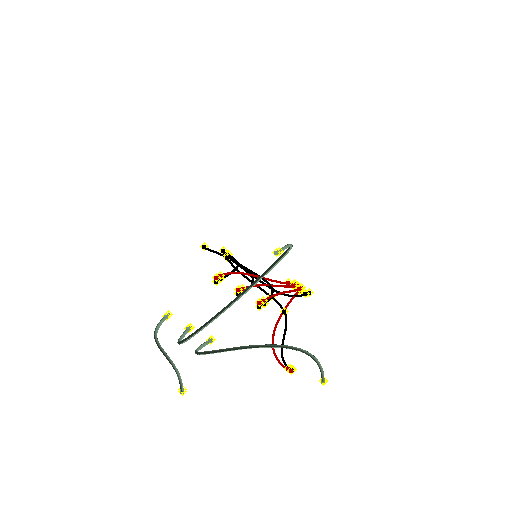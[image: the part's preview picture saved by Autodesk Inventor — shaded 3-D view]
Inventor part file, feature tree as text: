
AUTODESK INVENTOR PART (.ipt)
format: ipt  version: 2022 (Build 260153000, 153)  size: 630,272 bytes
history: native  units: mm (DEFAULTED — no unit token found)
features: other x74, plane x12, sketch x12, sweep x12
ambient origin geometry x8: Origin, YZ Plane, XZ Plane, XY Plane, X Axis, Y Axis, Z Axis, Center Point
bodies: Body1 (feature_tree), Body2 (feature_tree), Body3 (feature_tree), Body4 (feature_tree), Body5 (feature_tree), Body6 (feature_tree), Body7 (feature_tree), Body8 (feature_tree), Body9 (feature_tree), Body10 (feature_tree), Body11 (feature_tree), Body12 (feature_tree)
feature tree (110):
  other  "Work Point1"
  other  "Work Point2"
  other  "Wire1"
  other  "Work Point3"
  other  "Work Point4"
  other  "Wire2"
  other  "Work Point5"
  other  "Work Point6"
  other  "Wire3"
  other  "Work Point7"
  other  "Work Point8"
  other  "Work Point9"
  other  "Work Point10"
  other  "Work Point11"
  other  "Work Point12"
  plane  "Work Plane1"
  plane  "Work Plane2"
  plane  "Work Plane3"
  other  "Work Point13"
  other  "Work Point14"
  other  "Wire4"
  other  "Work Point15"
  other  "Work Point16"
  other  "Wire5"
  other  "Work Point17"
  other  "Work Point18"
  other  "Wire6"
  other  "Work Point19"
  other  "Work Point20"
  other  "Wire7"
  other  "Work Point21"
  other  "Work Point22"
  other  "Wire8"
  other  "Work Point23"
  other  "Work Point24"
  other  "Wire9"
  plane  "Work Plane4"
  plane  "Work Plane5"
  plane  "Work Plane6"
  plane  "Work Plane7"
  plane  "Work Plane8"
  plane  "Work Plane9"
  other  "Work Point25"
  other  "Work Point26"
  other  "Work Point27"
  other  "Work Point28"
  other  "Work Point29"
  other  "Work Point30"
  other  "Work Point31"
  other  "Work Point32"
  other  "Work Point33"
  other  "Work Point34"
  other  "Work Point35"
  other  "Work Point36"
  other  "Work Point37"
  other  "Work Point38"
  other  "Wire10"
  plane  "Work Plane10"
  other  "Work Point40"
  other  "Work Point41"
  other  "Work Point42"
  other  "Work Point43"
  other  "Wire11"
  other  "Work Point44"
  other  "Work Point45"
  other  "Wire12"
  other  "Work Point46"
  other  "Work Point47"
  other  "Work Point48"
  other  "Work Point49"
  plane  "Work Plane11"
  plane  "Work Plane12"
  other  "Work Point51"
  other  "Work Point52"
  sketch  "Sketch1"  dims[d0=0.0mm d1=0.0mm d2=0.0mm d3=0.0mm]
  other  "Srf1"
  sketch  "Sketch2"  dims[d4=0.0mm d5=0.0mm d6=0.0mm d7=0.0mm]
  other  "Srf2"
  sketch  "Sketch3"  dims[d8=0.0mm d9=0.0mm d10=0.0mm d11=0.0mm]
  other  "Srf3"
  sketch  "Sketch4"  dims[d12=0.0mm d13=0.0mm d14=0.0mm d15=0.0mm]
  other  "Srf4"
  sketch  "Sketch5"  dims[d16=0.0mm d17=0.0mm d18=0.0mm d19=0.0mm]
  other  "Srf5"
  sketch  "Sketch6"  dims[d20=0.0mm d21=0.0mm d22=0.0mm d23=0.0mm]
  other  "Srf6"
  sketch  "Sketch7"
  other  "Srf7"
  sketch  "Sketch8"
  other  "Srf8"
  sketch  "Sketch9"
  other  "Srf9"
  sketch  "Sketch10"
  other  "Srf10"
  sketch  "Sketch11"
  other  "Srf11"
  sketch  "Sketch12"
  other  "Srf12"
  sweep  "SweepSrf1"
  sweep  "SweepSrf2"
  sweep  "SweepSrf3"
  sweep  "SweepSrf4"
  sweep  "SweepSrf5"
  sweep  "SweepSrf6"
  sweep  "SweepSrf7"
  sweep  "SweepSrf8"
  sweep  "SweepSrf9"
  sweep  "SweepSrf10"
  sweep  "SweepSrf11"
  sweep  "SweepSrf12"
